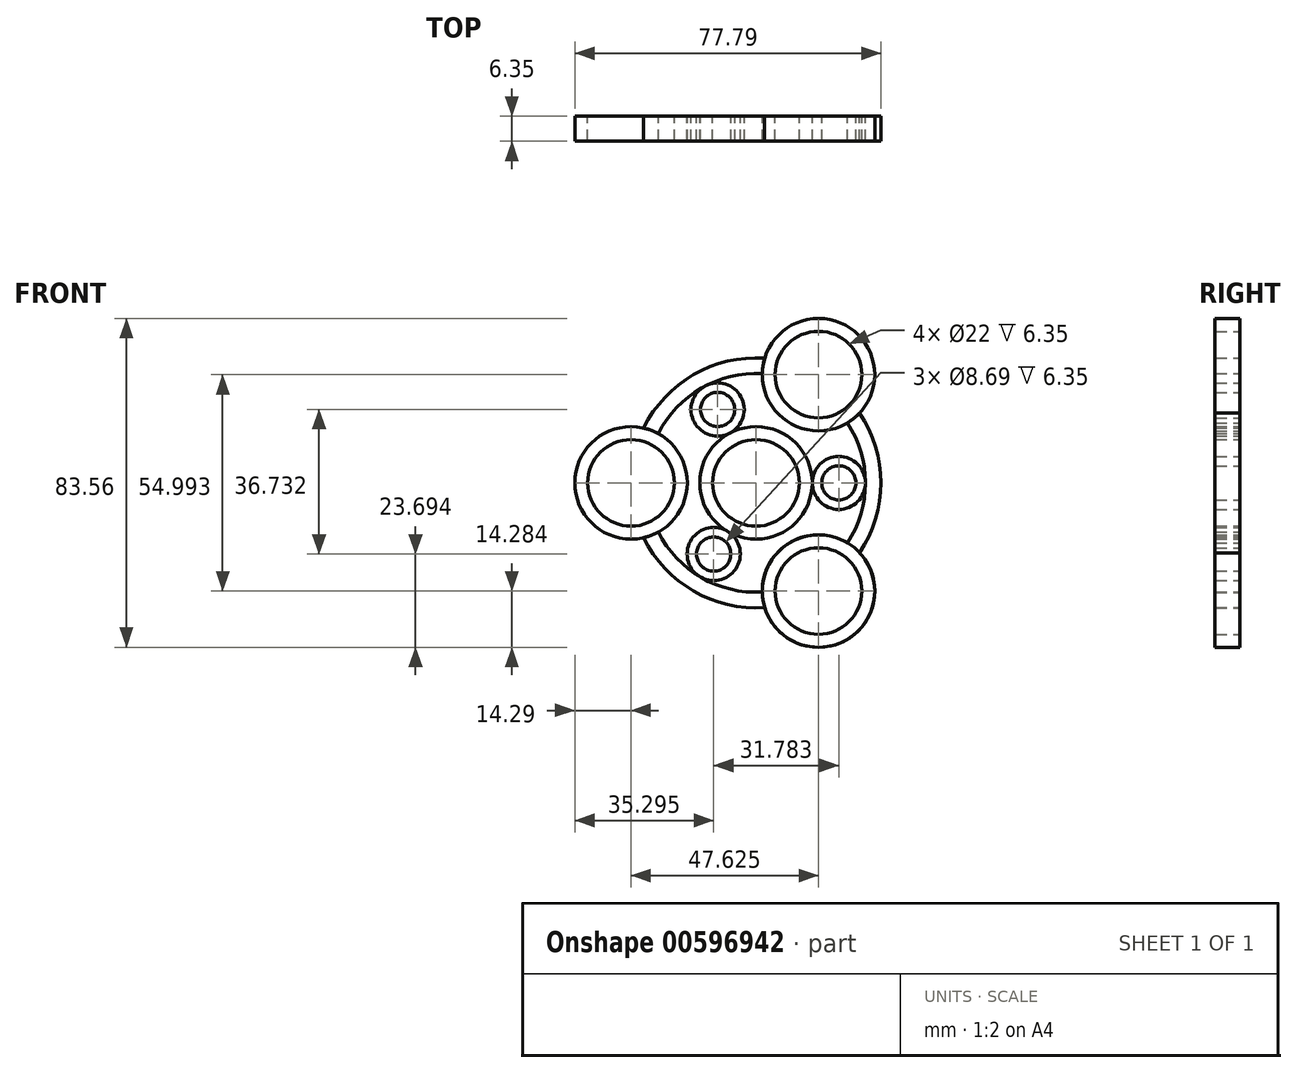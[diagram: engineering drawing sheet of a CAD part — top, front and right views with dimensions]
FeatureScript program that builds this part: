
annotation { "Feature Type Name" : "Feature", "Feature Type Description" : "" }
export const myFeature = defineFeature(function(context is Context, id is Id, definition is map)
    precondition{}
    {
        {
            var Q0;
            Q0=qCreatedBy(makeId("Front.planeOp"),FACE);
            var sketch = newSketch(context, id + "F0", { "sketchPlane" : qUnion([Q0])});
            skCircle(sketch, "E0", {"center": v(0, 0) * mm, "radius": 14.29 * mm});
            skCircle(sketch, "E1", {"center": v(0, 0) * mm, "radius": 11 * mm});
            skCircle(sketch, "E2", {"center": v(-31.75, 0) * mm, "radius": 14.29 * mm});
            skCircle(sketch, "E3", {"center": v(-31.75, 0) * mm, "radius": 11 * mm});
            skCircle(sketch, "E4.1.0", {"center": v(15.87, -27.5) * mm, "radius": 14.29 * mm});
            skCircle(sketch, "E4.1.1", {"center": v(15.87, -27.5) * mm, "radius": 11 * mm});
            skCircle(sketch, "E4.2.0", {"center": v(15.88, 27.5) * mm, "radius": 14.29 * mm});
            skCircle(sketch, "E4.2.1", {"center": v(15.88, 27.5) * mm, "radius": 11 * mm});
            skSolve(sketch);
        }
        {
            var Q0;
            Q0=qCreatedBy(makeId("Front.planeOp"),FACE);
            var sketch = newSketch(context, id + "F1", { "sketchPlane" : qUnion([Q0])});
            skArc(sketch, "E5", {"start": v(2.21, 31.67) * mm, "mid": v(-15.87, 27.5) * mm, "end": v(-28.54, 13.92) * mm});
            skArc(sketch, "E6", {"start": v(1.59, 27.74) * mm, "mid": v(-13.9, 24.06) * mm, "end": v(-24.82, 12.5) * mm});
            skCircle(sketch, "E7.2", {"center": v(15.88, 27.5) * mm, "radius": 14.29 * mm});
            skCircle(sketch, "E7.3", {"center": v(15.88, 27.5) * mm, "radius": 11 * mm});
            skCircle(sketch, "E7.4", {"center": v(-31.75, 0) * mm, "radius": 14.29 * mm});
            skCircle(sketch, "E7.5", {"center": v(-31.75, 0) * mm, "radius": 11 * mm});
            skCircle(sketch, "E7.6", {"center": v(0, 0) * mm, "radius": 14.29 * mm});
            skCircle(sketch, "E7.7", {"center": v(0, 0) * mm, "radius": 11 * mm});
            skArc(sketch, "E7.8", {"start": v(21.25, -17.9) * mm, "mid": v(8.86, -35.96) * mm, "end": v(24.3, -20.43) * mm});
            skArc(sketch, "E7.9", {"start": v(2.21, -31.67) * mm, "mid": v(29.99, -25.26) * mm, "end": v(1.59, -27.74) * mm});
            skCircle(sketch, "E8", {"center": v(-9.74, 18.65) * mm, "radius": 6.75 * mm});
            skCircle(sketch, "E9", {"center": v(-9.74, 18.65) * mm, "radius": 4.34 * mm});
            skCircle(sketch, "E10", {"center": v(21.04, 0) * mm, "radius": 6.75 * mm});
            skCircle(sketch, "E11", {"center": v(21.04, 0) * mm, "radius": 4.34 * mm});
            skCircle(sketch, "E12", {"center": v(-10.75, -18.09) * mm, "radius": 6.75 * mm});
            skCircle(sketch, "E13", {"center": v(-10.75, -18.09) * mm, "radius": 4.34 * mm});
            skArc(sketch, "E14.trimOffspring", {"start": v(-28.54, -13.92) * mm, "mid": v(-15.88, -27.5) * mm, "end": v(2.21, -31.67) * mm});
            skArc(sketch, "E15.trimOffspring", {"start": v(-24.82, -12.5) * mm, "mid": v(-13.9, -24.06) * mm, "end": v(1.59, -27.74) * mm});
            skArc(sketch, "E16.trimOffspring", {"start": v(23.23, -15.25) * mm, "mid": v(27.79, 0) * mm, "end": v(23.23, 15.25) * mm});
            skArc(sketch, "E17.trimOffspring", {"start": v(26.32, -17.75) * mm, "mid": v(31.75, 0) * mm, "end": v(26.32, 17.75) * mm});
            skSolve(sketch);
        }
        {
            var Q0;
            Q0=makeQuery(id+"F0.imprint","IMPRINT",FACE,{"disambiguationData":[TD([[makeQuery(id+"F0.imprint","IMPRINT",EDGE,{"derivedFrom":sQuery(id+"F0.wireOp",EDGE,"E2")}),1.0]])]});
            var Q1;
            Q1=makeQuery(id+"F0.imprint","IMPRINT",FACE,{"disambiguationData":[TD([[makeQuery(id+"F0.imprint","IMPRINT",EDGE,{"derivedFrom":sQuery(id+"F0.wireOp",EDGE,"E4.1.0")}),1.0]])]});
            var Q2;
            {var subQ8=sQuery(id+"F1.wireOp",EDGE,"E14.trimOffspring");Q2=makeQuery(id+"F1.imprint","IMPRINT",FACE,{"disambiguationData":[TD([[makeQuery(id+"F1.imprint","IMPRINT",EDGE,{"derivedFrom":subQ8}),1.0]])]});}
            var Q3;
            Q3=makeQuery(id+"F1.imprint","IMPRINT",FACE,{"disambiguationData":[TD([[makeQuery(id+"F1.imprint","IMPRINT",EDGE,{"derivedFrom":sQuery(id+"F1.wireOp",EDGE,"E13")}),-1.0]])]});
            var Q4;
            Q4=makeQuery(id+"F0.imprint","IMPRINT",FACE,{"disambiguationData":[TD([[makeQuery(id+"F0.imprint","IMPRINT",EDGE,{"derivedFrom":sQuery(id+"F0.wireOp",EDGE,"E1")}),-1.0]])]});
            var Q5;
            Q5=makeQuery(id+"F1.imprint","IMPRINT",FACE,{"disambiguationData":[TD([[makeQuery(id+"F1.imprint","IMPRINT",EDGE,{"derivedFrom":sQuery(id+"F1.wireOp",EDGE,"E11")}),-1.0]])]});
            var Q6;
            {var subQ6=sQuery(id+"F1.wireOp",EDGE,"E17.trimOffspring");Q6=makeQuery(id+"F1.imprint","IMPRINT",FACE,{"disambiguationData":[TD([[makeQuery(id+"F1.imprint","IMPRINT",EDGE,{"derivedFrom":subQ6}),1.0]])]});}
            var Q7;
            Q7=makeQuery(id+"F0.imprint","IMPRINT",FACE,{"disambiguationData":[TD([[makeQuery(id+"F0.imprint","IMPRINT",EDGE,{"derivedFrom":sQuery(id+"F0.wireOp",EDGE,"E4.2.0")}),1.0]])]});
            var Q8;
            Q8=makeQuery(id+"F1.imprint","IMPRINT",FACE,{"disambiguationData":[TD([[makeQuery(id+"F1.imprint","IMPRINT",EDGE,{"derivedFrom":sQuery(id+"F1.wireOp",EDGE,"E9")}),-1.0]])]});
            var Q9;
            {var subQ6=sQuery(id+"F1.wireOp",EDGE,"E5");Q9=makeQuery(id+"F1.imprint","IMPRINT",FACE,{"disambiguationData":[TD([[makeQuery(id+"F1.imprint","IMPRINT",EDGE,{"derivedFrom":subQ6}),1.0]])]});}
            extrude(context, id + "F2", {"entities" : qUnion([Q0, Q1, Q2, Q3, Q4, Q5, Q6, Q7, Q8, Q9]), "depth" : 6.35 * mm, "offsetDistance" : 25.4 * mm});
        }
    });
